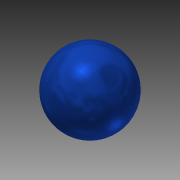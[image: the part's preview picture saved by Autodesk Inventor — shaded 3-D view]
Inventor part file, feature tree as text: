
AUTODESK INVENTOR PART (.ipt)
format: ipt  version: 2014 SP1 (Build 180222100, 222)  size: 114,176 bytes
history: native  units: in
note: dims shown in document units (in); Inventor stores cm internally (conversion verified against a paired STEP export)
features: revolve x1, sketch x1
ambient origin geometry x8: Origin, YZ Plane, XZ Plane, XY Plane, X Axis, Y Axis, Z Axis, Center Point
bodies: Solid1 (feature_tree)
feature tree (2):
  revolve  "Revolution1"  [1 undecoded]
  sketch  "Sketch1"  dims[d0=24.0in d1=24.0in d2=90.0deg]
note: 1 required parameter value undecoded (feature->parameter linkage not recoverable at this tier; creation-order binding heuristic only, values carry confidence <= 0.55)
